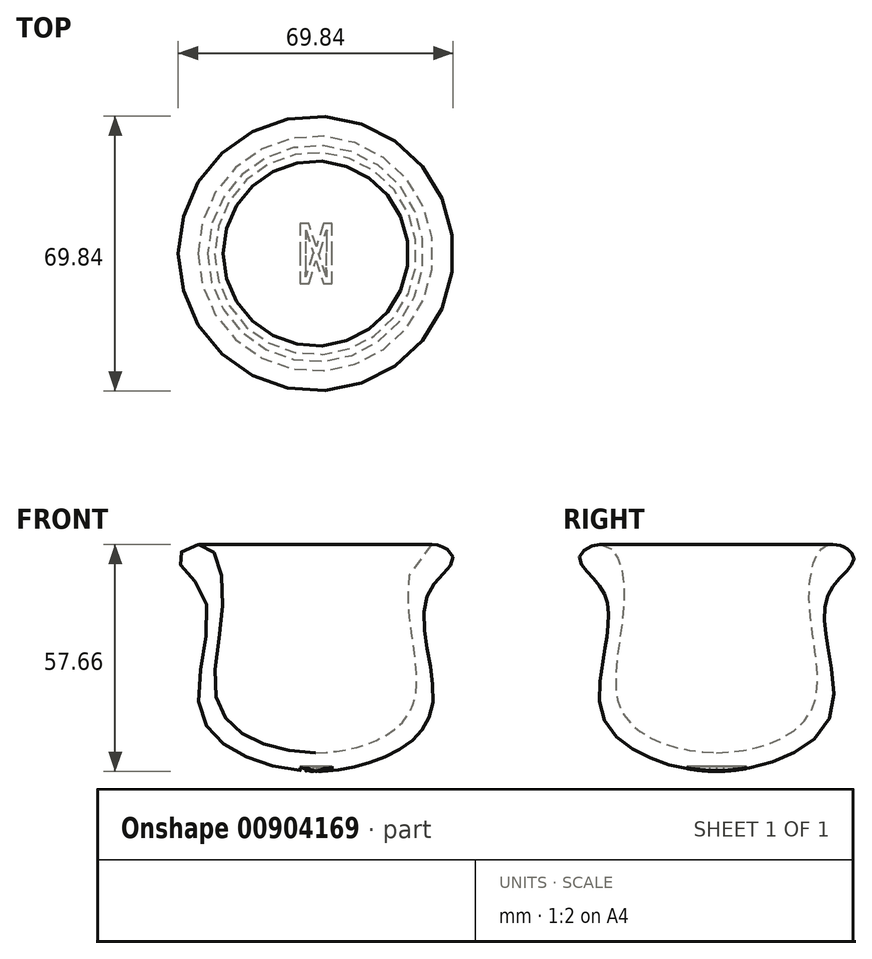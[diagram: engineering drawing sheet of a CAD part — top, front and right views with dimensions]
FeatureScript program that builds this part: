
annotation { "Feature Type Name" : "Feature", "Feature Type Description" : "" }
export const myFeature = defineFeature(function(context is Context, id is Id, definition is map)
    precondition{}
    {
        {
            var Q0;
            Q0=qCreatedBy(makeId("Front.planeOp"),FACE);
            var sketch = newSketch(context, id + "F0", { "sketchPlane" : qUnion([Q0])});
            skLineSegment(sketch, "E0", {"start": v(-28.58, 0) * mm, "end": v(28.58, 0) * mm, "construction": true});
            skLineSegment(sketch, "E1", {"start": v(0, 0) * mm, "end": v(0, -50.8) * mm, "construction": true});
            skLineSegment(sketch, "E2", {"start": v(-12.7, -50.8) * mm, "end": v(12.7, -50.8) * mm, "construction": true});
            skLineSegment(sketch, "E3", {"start": v(0, 0) * mm, "end": v(0, -12.7) * mm, "construction": true});
            skLineSegment(sketch, "E4", {"start": v(-23.5, -12.7) * mm, "end": v(23.5, -12.7) * mm, "construction": true});
            skLineSegment(sketch, "E5", {"start": v(0, -50.8) * mm, "end": v(0, -38.1) * mm, "construction": true});
            skLineSegment(sketch, "E6", {"start": v(-25.4, -38.1) * mm, "end": v(25.4, -38.1) * mm, "construction": true});
            skLineSegment(sketch, "E7", {"start": v(0, -52.8) * mm, "end": v(0, -57.57) * mm, "construction": true});
            skLineSegment(sketch, "E8", {"start": v(-19.77, -52.8) * mm, "end": v(-17.38, -48.69) * mm, "construction": true});
            skLineSegment(sketch, "E9", {"start": v(-28.25, -13.02) * mm, "end": v(-23.5, -12.7) * mm, "construction": true});
            skLineSegment(sketch, "E10", {"start": v(23.5, -12.7) * mm, "end": v(28.25, -12.93) * mm, "construction": true});
            skLineSegment(sketch, "E11", {"start": v(-25.4, -38.1) * mm, "end": v(-29.76, -40.01) * mm, "construction": true});
            skLineSegment(sketch, "E12", {"start": v(25.4, -38.1) * mm, "end": v(30.07, -39.03) * mm, "construction": true});
            skLineSegment(sketch, "E13", {"start": v(16.77, -49.02) * mm, "end": v(19.05, -53.2) * mm, "construction": true});
            skLineSegment(sketch, "E14", {"start": v(-28.58, 0) * mm, "end": v(-34.9, -3.29) * mm, "construction": true});
            skLineSegment(sketch, "E15", {"start": v(28.58, 0) * mm, "end": v(34.58, -3.85) * mm, "construction": true});
            skLineSegment(sketch, "E16", {"start": v(0, -52.8) * mm, "end": v(0, -57.57) * mm});
            skFitSpline(sketch, "E17", {"points": [v(0, -57.57) * mm, v(19.05, -53.2) * mm, v(30.07, -39.03) * mm, v(28.25, -12.93) * mm, v(34.58, -3.85) * mm, v(28.57, 0) * mm, v(23.5, -12.7) * mm, v(25.4, -38.1) * mm, v(16.77, -49.02) * mm, v(0, -52.8) * mm, v(-17.38, -48.69) * mm, v(-25.4, -38.1) * mm, v(-23.5, -12.7) * mm, v(-28.57, 0) * mm, v(-34.9, -3.29) * mm, v(-28.25, -13.02) * mm, v(-29.76, -40.01) * mm, v(-19.77, -52.8) * mm, v(0, -57.57) * mm]});
            skLineSegment(sketch, "E18", {"start": v(0, -57.57) * mm, "end": v(-12.7, -57.57) * mm, "construction": true});
            skLineSegment(sketch, "E19", {"start": v(0, -57.57) * mm, "end": v(12.7, -57.57) * mm, "construction": true});
            skLineSegment(sketch, "E20", {"start": v(-12.7, -57.57) * mm, "end": v(12.7, -57.57) * mm});
            skLineSegment(sketch, "E21", {"start": v(-12.7, -57.57) * mm, "end": v(-12.7, -58.84) * mm});
            skLineSegment(sketch, "E22", {"start": v(-12.7, -58.84) * mm, "end": v(12.7, -58.84) * mm});
            skLineSegment(sketch, "E23", {"start": v(12.7, -58.84) * mm, "end": v(12.7, -57.57) * mm});
            skLineSegment(sketch, "E24", {"start": v(-25.12, -3.29) * mm, "end": v(25.11, -3.29) * mm, "construction": true});
            skLineSegment(sketch, "E25", {"start": v(-32.45, -0.62) * mm, "end": v(31.8, -0.62) * mm, "construction": true});
            skSolve(sketch);
        }
        {
            var Q0;
            {var subQ0=sQuery(id+"F0.wireOp",EDGE,"E16");Q0=makeQuery(id+"F0.imprint","IMPRINT",FACE,{"disambiguationData":[TD([[makeQuery(id+"F0.imprint","IMPRINT",EDGE,{"derivedFrom":subQ0}),-1.0]])]});}
            var Q1;
            Q1=sQuery(id+"F0.wireOp",EDGE,"E3");
            revolve(context, id + "F1", {"surfaceOperationType" : NewSurfaceOperationType.NEW, "entities" : qUnion([Q0]), "axis" : qUnion([Q1]), "revolveType" : RevolveType.FULL});
        }
        {
            var Q0;
            {var subQ0=sQuery(id+"F0.wireOp",EDGE,"E21");Q0=makeQuery(id+"F0.imprint","IMPRINT",FACE,{"disambiguationData":[TD([[makeQuery(id+"F0.imprint","IMPRINT",EDGE,{"derivedFrom":subQ0}),1.0]])]});}
            extrude(context, id + "F2", {"entities" : qUnion([Q0]), "endBound" : BoundingType.SYMMETRIC, "depth" : 25.4 * mm, "offsetDistance" : 25.4 * mm});
        }
        {
            var Q0;
            Q0=makeQuery(id+"F2.opExtrude","SWEPT_FACE",FACE,{"disambiguationData":[OSD([sQuery(id+"F0.wireOp",EDGE,"E22")])]});
            var sketch = newSketch(context, id + "F3", { "sketchPlane" : qUnion([Q0])});
            skText(sketch, "E26", { "text": "M", "fontName": "OpenSans-Bold.ttf"});
            skText(sketch, "E27", { "text": "M", "fontName": "OpenSans-Bold.ttf"});
            const initialGuessF3  = {"E26": [-0.00487, 0, 1, 0, 0.00764], "E27": [0.00512, 0, -1, 0, 0.00764]};
            skSetInitialGuess(sketch, initialGuessF3);
            skSolve(sketch);
        }
        {
            var Q0;
            Q0=makeQuery(id+"F3.imprint","IMPRINT",FACE,{"disambiguationData":[TD([[makeQuery(id+"F3.imprint","IMPRINT",EDGE,{"derivedFrom":sQuery(id+"F3.wireOp",EDGE,"E27.sketch_text.stroke-0")}),-1.0]])]});
            var Q1;
            Q1=makeQuery(id+"F3.imprint","IMPRINT",FACE,{"disambiguationData":[TD([[makeQuery(id+"F3.imprint","IMPRINT",EDGE,{"derivedFrom":sQuery(id+"F3.wireOp",EDGE,"E26.sketch_text.stroke-0")}),-1.0]])]});
            extrude(context, id + "F4", {"entities" : qUnion([Q0, Q1]), "operationType" : NewBodyOperationType.REMOVE, "oppositeDirection" : true, "depth" : 2.54 * mm, "offsetDistance" : 25.4 * mm});
        }
        {
            var Q0;
            Q0=makeQuery(id+"F2.opExtrude","CAP_FACE",FACE,{"disambiguationData":[OSD([sQuery(id+"F0.wireOp",EDGE,"E17"),sQuery(id+"F0.wireOp",EDGE,"E20"),sQuery(id+"F0.wireOp",EDGE,"E21"),sQuery(id+"F0.wireOp",EDGE,"E22"),sQuery(id+"F0.wireOp",EDGE,"E23")])],"isStart":false});
            extrude(context, id + "F5", {"entities" : qUnion([Q0]), "operationType" : NewBodyOperationType.REMOVE, "endBound" : BoundingType.THROUGH_ALL, "oppositeDirection" : true, "depth" : 25.4 * mm, "offsetDistance" : 25.4 * mm});
        }
    });
